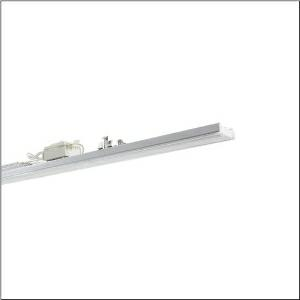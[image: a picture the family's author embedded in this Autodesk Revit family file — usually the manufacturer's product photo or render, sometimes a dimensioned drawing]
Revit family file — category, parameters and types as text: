
# Revit family: licross_r__11_recessed_ho_51te12dn4exm3c_0300
name_source: partatom
category: Lighting Fixtures
units: mm (PartAtom-declared; Revit-internal decimal feet)

## family parameters
Cut with Voids When Loaded = No
Host = Face
Light Source = No
Part Type = Normal
Room Calculation Point = No
Round Connector Dimension = Use Diameter
Shared = No

## types (1)
- --- (1 x LED, 1000 lm, 7.2 W, 4000K)
    Apparent Load = 7 VA
    CIE Flux Codes = 66 91 98 100 100
    Color Rendering = 80
    Color Temperature = 4000K
    Default Elevation = 1800 mm
    Description = Licross® 11 Recessed HO, luminaire insert, of sheet steel, galvanised, coil coated, white, length: 1.500mm, width: 66mm, height: 67mm, LED rated luminous flux: 14.030lm, light colour: 840, control gear: DALI 2 (for two DALI lines), with plug, 6-pole, with phase selection, for trunking rail, 14-core, mains connection: 220..240V, AC, 50/60Hz, rated input power: 81W, for trunking rail, 14-core, halogen-free wiring, for emergency light function, converter,control gear: single battery element, battery: LiFePO4, 9Ah, primary optical cover: cover, of PMMA, light emission: direct distribution, primary light characteristic: symmetric, protection rating (complete): IP54, insulation class (complete): insulation class I (protective earthing), certification: CE, UKCA, protection symbol: D if used in an environment with non-conductive dust loads with corresponding accessories, impact resistance: IK06, permissible ambient temperature for indoor applications: +5..+30°C, standard: EN 60598-2-22, LABS conformity tested according to VDMA 24364:2018-05, reducing of maximum allowable ambient temperature of 5°C with ceiling mounting, corresponds to IFS (International Featured Standards) requirements for safety and quality in the food industry, packaging unit: 1 piece
    Height = 58 mm
    Lamp = 1 x LED
    Lamp Light Flux = 1000 lm
    Lamp Power = 7.2 W
    Lamp count = 1
    Length = 1500 mm
    Luminous efficacy = 139 lm/W
    Manufacturer = Siteco
    ModVariant = No
    Model = 51TE12DN4EXM3C
    Mounting Place = Ceiling
    Mounting Type = Pendant
    Number of Poles = 1
    OnlyDefault = Yes
    Power Factor = 1
    Product Name = Licross® 11 Recessed HO
    Product group = luminaire insert
    ProductGroupID = 902
    Protection Class = Protection class I
    Protection Degree = IP 54
    RLX_Detail_Level = 1
    RLX_Emergency_Light_Flux = 0 lm
    RLX_Emergency_Type = 0
    RLX_Emergency_Type_DB = No
    RlxData = <blob elided: 25005 chars, md5=8908c35b>
    Socket = socket
    Standby Power = 0 W
    System Light Flux = 1000 lm
    System Power = 7 W
    Type Comments = : emergency light operation: 3 h
    Type Image = l_1296930.jpg
    URL = http://relux.com
    VarID = @adj_089912
    Voltage = 0 V
    Weight = 0.00 kg
    Width = 66 mm

## geometry (parser evidence)
native form markers: Blend x4, Sweep x12
no freeform markers — native parametric forms only
